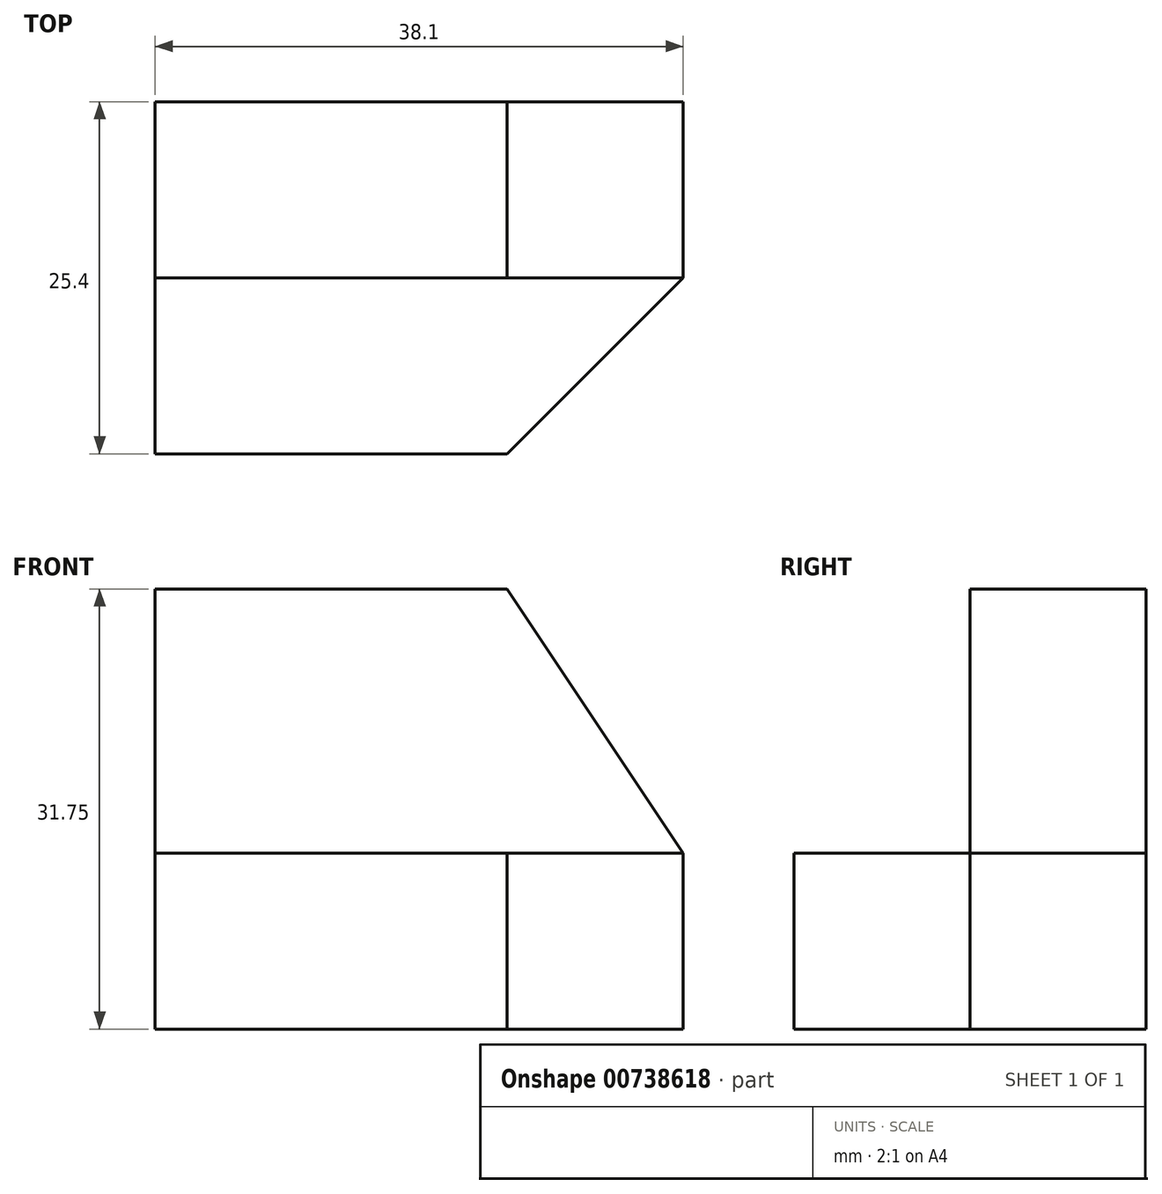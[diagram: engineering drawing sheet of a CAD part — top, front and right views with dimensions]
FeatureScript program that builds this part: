
annotation { "Feature Type Name" : "Feature", "Feature Type Description" : "" }
export const myFeature = defineFeature(function(context is Context, id is Id, definition is map)
    precondition{}
    {
        {
            var Q0;
            Q0=qCreatedBy(makeId("Top.planeOp"),FACE);
            var sketch = newSketch(context, id + "F0", { "sketchPlane" : qUnion([Q0])});
            skLineSegment(sketch, "E0.bottom", {"start": v(0, 0) * mm, "end": v(38.1, 0) * mm});
            skLineSegment(sketch, "E0.top", {"start": v(0, 25.4) * mm, "end": v(38.1, 25.4) * mm});
            skLineSegment(sketch, "E0.left", {"start": v(0, 0) * mm, "end": v(0, 25.4) * mm});
            skLineSegment(sketch, "E0.right", {"start": v(38.1, 0) * mm, "end": v(38.1, 25.4) * mm});
            skLineSegment(sketch, "E1", {"start": v(0, 0) * mm, "end": v(25.4, 0) * mm});
            skLineSegment(sketch, "E2", {"start": v(38.1, 25.4) * mm, "end": v(38.1, 12.7) * mm});
            skLineSegment(sketch, "E3", {"start": v(25.4, 0) * mm, "end": v(38.1, 12.7) * mm});
            skSolve(sketch);
        }
        {
            var Q0;
            {var subQ1=sQuery(id+"F0.wireOp",EDGE,"E0.top");Q0=makeQuery(id+"F0.imprint","IMPRINT",FACE,{"disambiguationData":[TD([[makeQuery(id+"F0.imprint","IMPRINT",EDGE,{"derivedFrom":subQ1}),-1.0]])]});}
            extrude(context, id + "F1", {"entities" : qUnion([Q0]), "depth" : 12.7 * mm, "offsetDistance" : 25.4 * mm});
        }
        {
            var Q0;
            Q0=makeQuery(id+"F1.opExtrude","CAP_FACE",FACE,{"disambiguationData":[OSD([sQuery(id+"F0.wireOp",EDGE,"E0.bottom"),sQuery(id+"F0.wireOp",EDGE,"E0.top"),sQuery(id+"F0.wireOp",EDGE,"E0.left"),sQuery(id+"F0.wireOp",EDGE,"E0.right"),sQuery(id+"F0.wireOp",EDGE,"E3")])],"isStart":false});
            var sketch = newSketch(context, id + "F2", { "sketchPlane" : qUnion([Q0])});
            skLineSegment(sketch, "E4", {"start": v(38.1, 12.7) * mm, "end": v(0, 12.7) * mm});
            skSolve(sketch);
        }
        {
            var Q0;
            {var subQ0=sQuery(id+"F2.wireOp",EDGE,"E4");Q0=makeQuery(id+"F2.imprint","IMPRINT",FACE,{"disambiguationData":[TD([[makeQuery(id+"F2.imprint","IMPRINT",EDGE,{"derivedFrom":subQ0}),-1.0]])]});}
            extrude(context, id + "F3", {"entities" : qUnion([Q0]), "operationType" : NewBodyOperationType.ADD, "depth" : 19.05 * mm, "offsetDistance" : 25.4 * mm});
        }
        {
            var Q0;
            Q0=makeQuery(id+"F3.opExtrude","SWEPT_FACE",FACE,{"disambiguationData":[OSD([sQuery(id+"F2.wireOp",EDGE,"E4")])]});
            var sketch = newSketch(context, id + "F4", { "sketchPlane" : qUnion([Q0])});
            skLineSegment(sketch, "E5", {"start": v(38.1, 12.7) * mm, "end": v(25.4, 31.75) * mm});
            skLineSegment(sketch, "E6", {"start": v(25.4, 31.75) * mm, "end": v(0, 31.75) * mm});
            skSolve(sketch);
        }
        {
            var Q0;
            {var subQ0=sQuery(id+"F4.wireOp",EDGE,"E5");Q0=makeQuery(id+"F4.imprint","IMPRINT",FACE,{"disambiguationData":[TD([[makeQuery(id+"F4.imprint","IMPRINT",EDGE,{"derivedFrom":subQ0}),-1.0]])]});}
            extrude(context, id + "F5", {"entities" : qUnion([Q0]), "operationType" : NewBodyOperationType.REMOVE, "oppositeDirection" : true, "depth" : 25.4 * mm, "offsetDistance" : 25.4 * mm});
        }
    });
